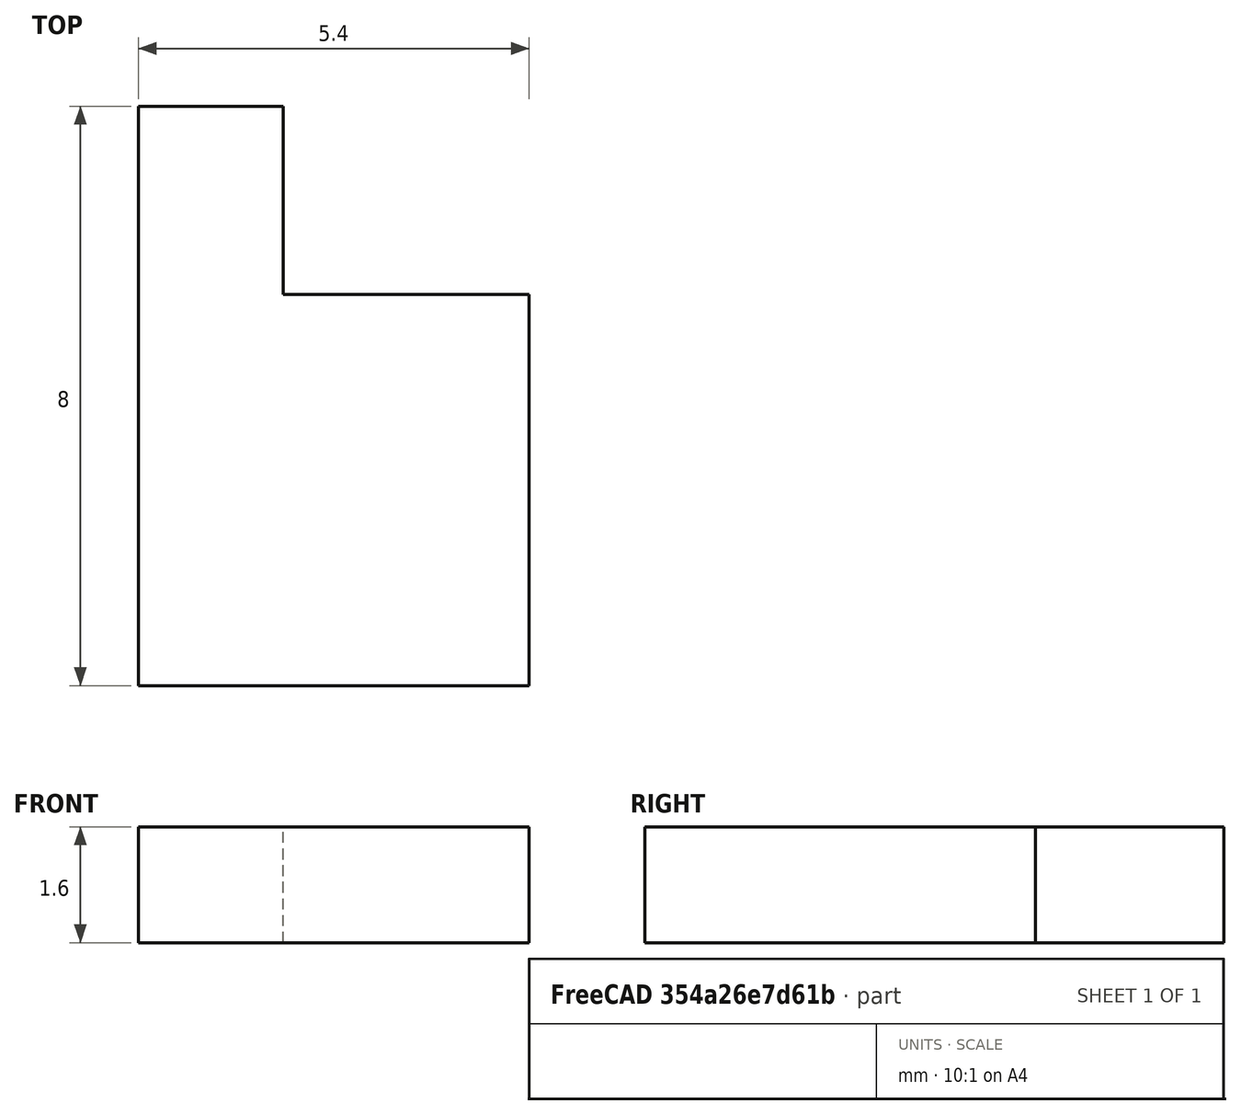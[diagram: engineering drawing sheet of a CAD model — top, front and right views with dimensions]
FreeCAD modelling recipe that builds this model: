
FCSTD DOCUMENT  (FreeCAD 0.21R33668 +26 (Git))
Label: resetButton
License: All rights reserved
LicenseURL: https://en.wikipedia.org/wiki/All_rights_reserved
objects: Sketcher::SketchObject×1, PartDesign::Pad×1, PartDesign::Body×1
note: 4 computed .brp shape members not serialized (recipe doc carries the construction recipe); baked Part::Feature solids carry a one-line shape summary decoded from their .brp

FEATURE [Sketcher::SketchObject] Sketch
  FullyConstrained = true
  MapMode = 5
  Support = -> [XY_Plane]
  sketch-geometry (6):
    g0: LineSegment StartX=0 StartY=8 StartZ=0 EndX=0 EndY=0 EndZ=0
    g1: LineSegment StartX=0 StartY=0 StartZ=0 EndX=5.4 EndY=0 EndZ=0
    g2: LineSegment StartX=5.4 StartY=0 StartZ=0 EndX=5.4 EndY=5.4 EndZ=0
    g3: LineSegment StartX=5.4 StartY=5.4 StartZ=0 EndX=2 EndY=5.4 EndZ=0
    g4: LineSegment StartX=2 StartY=5.4 StartZ=0 EndX=2 EndY=8 EndZ=0
    g5: LineSegment StartX=2 StartY=8 StartZ=0 EndX=0 EndY=8 EndZ=0
  constraints (17):
    c: Vertical(g0)
    c: Coincident(g1,g0)
    c: Horizontal(g1)
    c: Coincident(g2,g1)
    c: Vertical(g2)
    c: Coincident(g3,g2)
    c: Horizontal(g3)
    c: Coincident(g4,g3)
    c: Vertical(g4)
    c: Coincident(g5,g4)
    c: Coincident(g5,g0)
    c: Horizontal(g5)
    c: Distance(g1) = 5.4
    c: Distance(g5) = 2
    c: Distance(g0) = 8
    c: Distance(g2) = 5.4
    c: Coincident(g0,g-1)
FEATURE [PartDesign::Pad] Pad
  Direction = (0,0,1)
  Length = 1.6
  Length2 = 10
  Profile = -> Sketch
  ReferenceAxis = -> Sketch [N_Axis]
  Type = 0
FEATURE [PartDesign::Body] Body
  Group = -> [Sketch,Pad]
  Origin = -> Origin
  Tip = -> Pad
